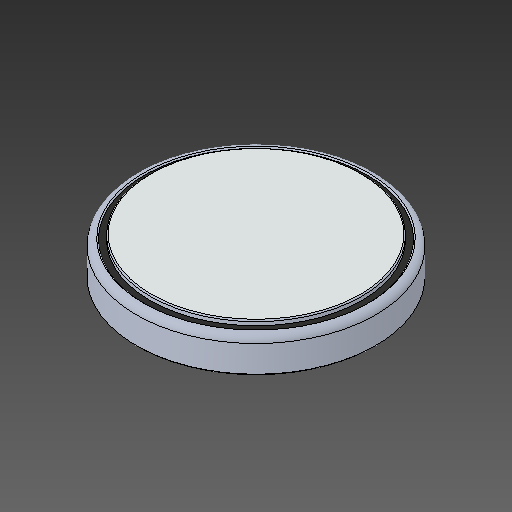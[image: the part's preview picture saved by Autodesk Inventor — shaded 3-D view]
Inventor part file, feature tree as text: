
AUTODESK INVENTOR PART (.ipt)
format: ipt  version: 2018.2 (Build 222227000, 227)  size: 130,560 bytes
history: native  units: mm
features: other x1, fillet x1
ambient origin geometry x8: Origin, YZ Plane, XZ Plane, XY Plane, X Axis, Y Axis, Z Axis, Center Point
bodies: Body1 (feature_tree)
feature tree (2):
  other  "ソリッド1"
  fillet  "Fillet1"  [1 undecoded]
note: 1 required parameter value undecoded (feature->parameter linkage not recoverable at this tier; creation-order binding heuristic only, values carry confidence <= 0.55)
